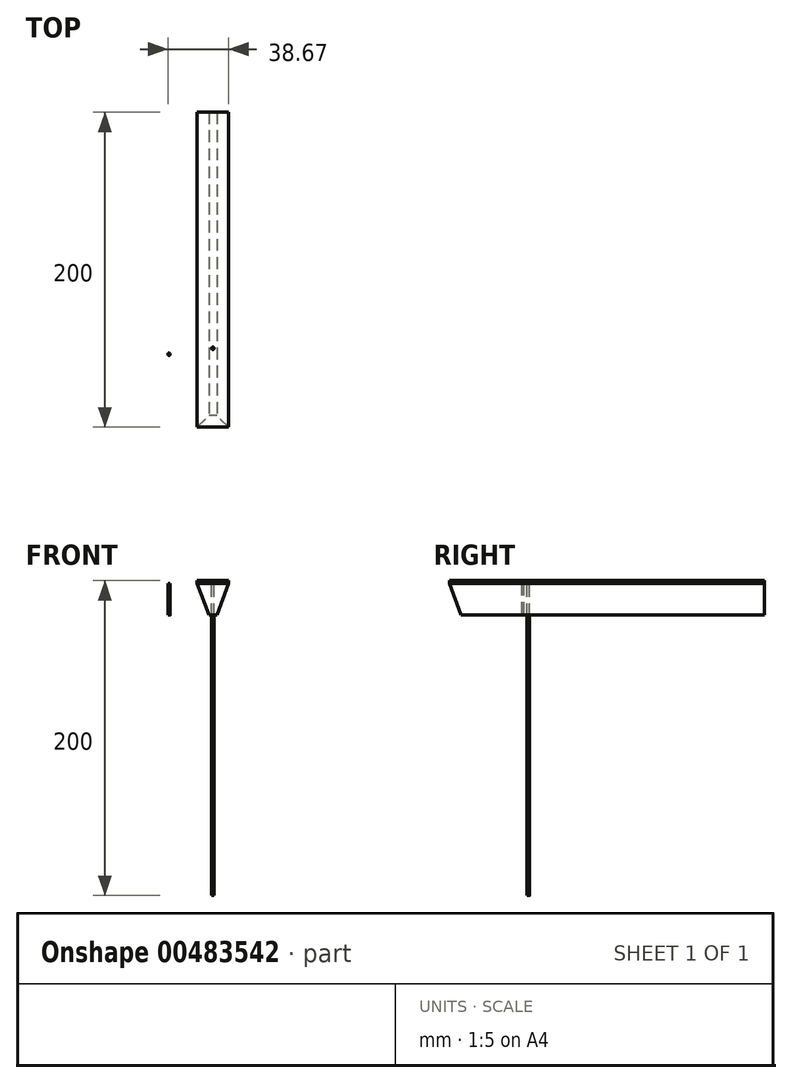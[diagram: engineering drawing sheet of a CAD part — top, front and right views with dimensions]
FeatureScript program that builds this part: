
annotation { "Feature Type Name" : "Feature", "Feature Type Description" : "" }
export const myFeature = defineFeature(function(context is Context, id is Id, definition is map)
    precondition{}
    {
        {
            var Q0;
            Q0=qCreatedBy(makeId("Top.planeOp"),FACE);
            var sketch = newSketch(context, id + "F0", { "sketchPlane" : qUnion([Q0])});
            skLineSegment(sketch, "E0.bottom", {"start": v(0, 0) * mm, "end": v(20, 0) * mm});
            skLineSegment(sketch, "E0.top", {"start": v(0, 200) * mm, "end": v(20, 200) * mm});
            skLineSegment(sketch, "E0.left", {"start": v(0, 0) * mm, "end": v(0, 200) * mm});
            skLineSegment(sketch, "E0.right", {"start": v(20, 0) * mm, "end": v(20, 200) * mm});
            skSolve(sketch);
        }
        {
            var Q0;
            Q0=qSketchRegion(id+"F0",true);
            extrude(context, id + "F1", {"entities" : qUnion([Q0]), "depth" : 20 * mm});
        }
        {
            var Q0;
            Q0=makeQuery(id+"F1.opExtrude","SWEPT_FACE",FACE,{"disambiguationData":[OSD([sQuery(id+"F0.wireOp",EDGE,"E0.bottom")])]});
            var sketch = newSketch(context, id + "F2", { "sketchPlane" : qUnion([Q0])});
            skLineSegment(sketch, "E1", {"start": v(0, 20) * mm, "end": v(7.5, 0) * mm});
            skLineSegment(sketch, "E2", {"start": v(7.5, 0) * mm, "end": v(0, 0) * mm});
            skLineSegment(sketch, "E3", {"start": v(0, 0) * mm, "end": v(0, 20) * mm});
            skLineSegment(sketch, "E4", {"start": v(12.5, 0) * mm, "end": v(20, 0) * mm});
            skLineSegment(sketch, "E5", {"start": v(20, 0) * mm, "end": v(20, 20) * mm});
            skLineSegment(sketch, "E6", {"start": v(20, 20) * mm, "end": v(12.5, 0) * mm});
            skSolve(sketch);
        }
        {
            var Q0;
            Q0=qSketchRegion(id+"F2",true);
            extrude(context, id + "F3", {"entities" : qUnion([Q0]), "operationType" : NewBodyOperationType.REMOVE, "endBound" : BoundingType.THROUGH_ALL, "oppositeDirection" : true, "depth" : 25 * mm});
        }
        {
            var Q0;
            Q0=qCreatedBy(makeId("Right.planeOp"),FACE);
            var sketch = newSketch(context, id + "F4", { "sketchPlane" : qUnion([Q0])});
            skLineSegment(sketch, "E7", {"start": v(0, 0) * mm, "end": v(0, 20) * mm});
            skLineSegment(sketch, "E8", {"start": v(0, 20) * mm, "end": v(7.28, 0) * mm});
            skLineSegment(sketch, "E9", {"start": v(7.28, 0) * mm, "end": v(0, 0) * mm});
            skSolve(sketch);
        }
        {
            var Q0;
            Q0=qSketchRegion(id+"F4",true);
            extrude(context, id + "F5", {"entities" : qUnion([Q0]), "operationType" : NewBodyOperationType.REMOVE, "endBound" : BoundingType.THROUGH_ALL, "depth" : 25 * mm});
        }
        {
            var Q0;
            Q0=makeQuery(id+"F1.opExtrude","CAP_FACE",FACE,{"disambiguationData":[OSD([sQuery(id+"F0.wireOp",EDGE,"E0.bottom"),sQuery(id+"F0.wireOp",EDGE,"E0.top"),sQuery(id+"F0.wireOp",EDGE,"E0.left"),sQuery(id+"F0.wireOp",EDGE,"E0.right")])],"isStart":false});
            var sketch = newSketch(context, id + "F6", { "sketchPlane" : qUnion([Q0])});
            skLineSegment(sketch, "E10.bottom", {"start": v(0, 0) * mm, "end": v(20, 0) * mm});
            skLineSegment(sketch, "E10.top", {"start": v(0, 200) * mm, "end": v(20, 200) * mm});
            skLineSegment(sketch, "E10.left", {"start": v(0, 0) * mm, "end": v(0, 200) * mm});
            skLineSegment(sketch, "E10.right", {"start": v(20, 0) * mm, "end": v(20, 200) * mm});
            skSolve(sketch);
        }
        {
            var Q0;
            Q0=qSketchRegion(id+"F6",true);
            extrude(context, id + "F7", {"entities" : qUnion([Q0]), "depth" : 2 * mm});
        }
        {
            var Q0;
            Q0=makeQuery(id+"F7.opExtrude","CAP_FACE",FACE,{"disambiguationData":[OSD([sQuery(id+"F6.wireOp",EDGE,"E10.bottom"),sQuery(id+"F6.wireOp",EDGE,"E10.top"),sQuery(id+"F6.wireOp",EDGE,"E10.left"),sQuery(id+"F6.wireOp",EDGE,"E10.right")])],"isStart":false});
            var sketch = newSketch(context, id + "F8", { "sketchPlane" : qUnion([Q0])});
            skCircle(sketch, "E11", {"center": v(10, 50) * mm, "radius": 0.8 * mm});
            skSolve(sketch);
        }
        {
            var Q0;
            Q0=qSketchRegion(id+"F8",true);
            extrude(context, id + "F9", {"entities" : qUnion([Q0]), "oppositeDirection" : true, "depth" : 200 * mm});
        }
        {
            var Q0;
            Q0=qCreatedBy(makeId("Top.planeOp"),FACE);
            var sketch = newSketch(context, id + "F10", { "sketchPlane" : qUnion([Q0])});
            skCircle(sketch, "E12", {"center": v(-17.92, 46.27) * mm, "radius": 0.75 * mm});
            skSolve(sketch);
        }
        {
            var Q0;
            Q0=qSketchRegion(id+"F10",true);
            extrude(context, id + "F11", {"entities" : qUnion([Q0]), "depth" : 20 * mm});
        }
    });
